# Revit family: CVSL-CM
name_source: partatom
category: Lighting Fixtures
revit_build: Autodesk Revit 2013 (Build: 20130531_2115(x64)
units: mm (PartAtom-declared; Revit-internal decimal feet)

## types (6) — shared parameters
Color Filter = 16777215
Default Elevation = 48"
Description = luminescent blades are placed along each side of an elegant curvature to create unparalleled aesthetics
Dimming Lamp Color Temperature Shift = <None>
Emit Shape Visible in Rendering = No
Emit from Rectangle Length = 46"
Emit from Rectangle Width = 7"
Glass = Hubbell - White Glass
Housing Material = Hubbell - White
Lamp = T5, T5HO, T8
Load Classification = Lighting
Manufacturer = Alera Lighting
Model = CVSL
Photometric Notes = More IES files download on Photometric Web Link
Photometric Web Link = https://www.hubbell.com
Power Factor = 1
Product Documentation Link = https://hubbellcdn.com
Product Page URL = https://www.hubbell.com
Row Length = 48"
Suspension Height = 24"
Tilt Angle = -90.00°
URL = https://www.hubbell.com
Voltage = 120 V

## per-type parameters (varying)
| type | Apparent Load | Distribution | Lamp Type | Photometric Web File | Watts |
| CVSL-4T8-50/50-E | 118 VA | 50% Uplight, 50% Downlight | Four T8 Lamps | CVSL-4T8-50 50-E.ies | 118 W |
| CVSL-3T5-70/30-EP | 183 VA | 70% Uplight, 30% Downlight | Three T5 Lamps | CVSL-3T5-70 30-EP.ies | 183 W |
| CVSL-2T5-40/60-EP | 116 VA | 40% Uplight, 60% Downlight | Two T5 Lamps | CVSL-2T5-40 60-EP.ies | 116 W |
| CVSL-3T8-50/50-E | 89 VA | 50% Uplight, 50% Downlight | Three T8 Lamps | CVSL-3T8-50 50-E.ies | 89 W |
| CVSL-4T5-40/60-EP | 232 VA | 40% Uplight, 60% Downlight | Four T5 Lamps | CVSL-4T5-40 60-EP.ies | 232 W |
| CVSL-2T8-50/50-E | 62 VA | 50% Uplight, 50% Downlight | Two T8 Lamp | CVSL-4T8-50 50-E.ies | 62 W |

## geometry (parser evidence)
native form markers: Blend x8, Sweep x3
no freeform markers — native parametric forms only
